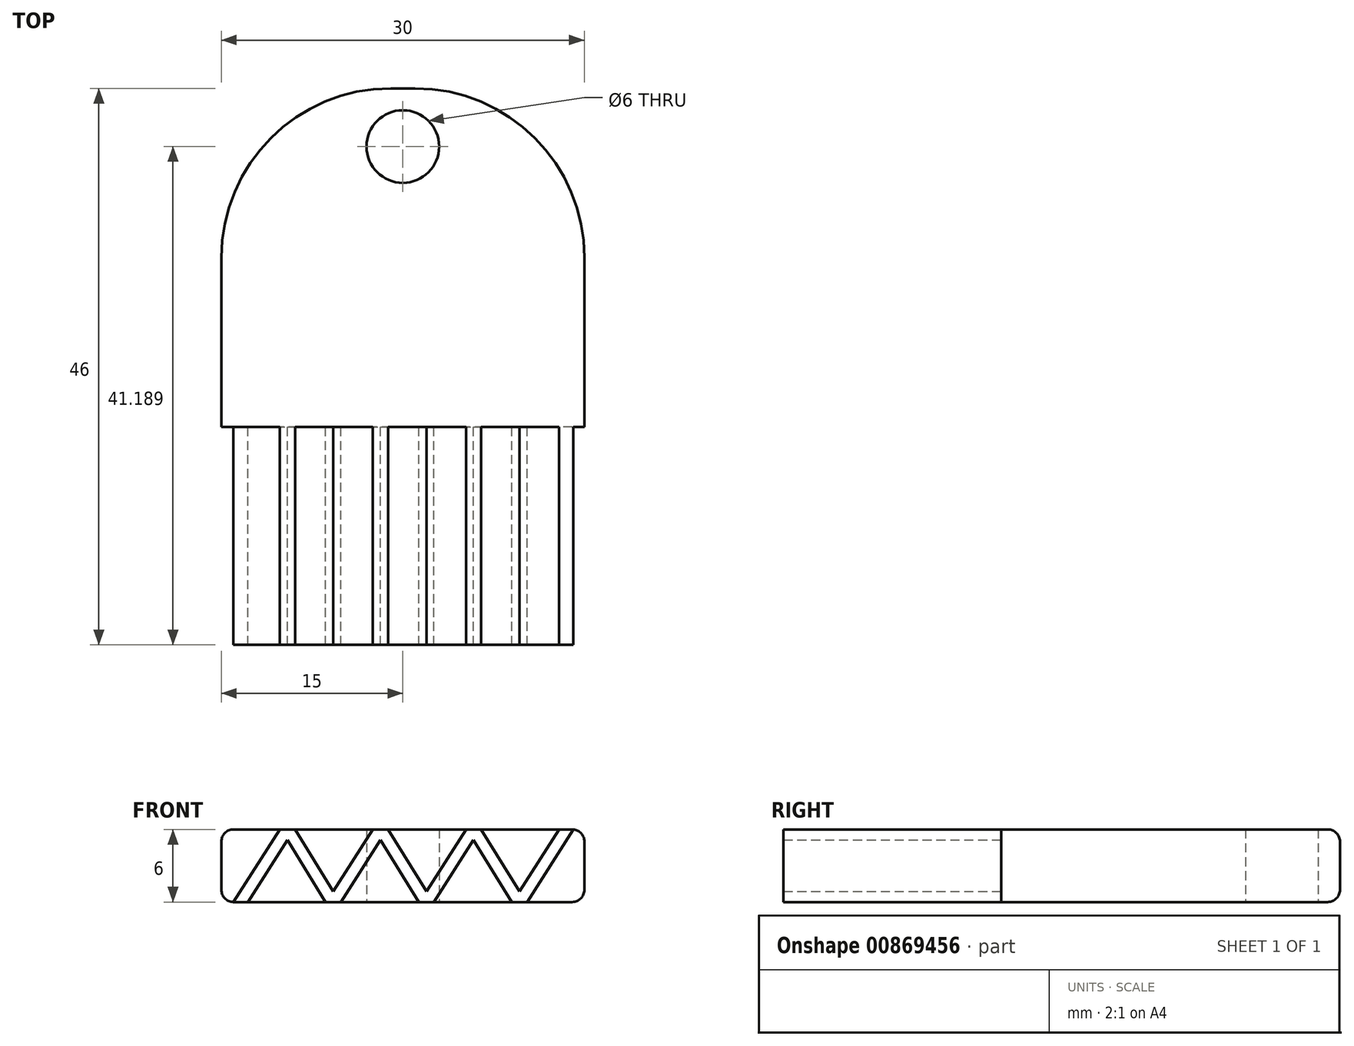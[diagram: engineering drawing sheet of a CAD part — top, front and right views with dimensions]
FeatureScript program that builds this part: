
annotation { "Feature Type Name" : "Feature", "Feature Type Description" : "" }
export const myFeature = defineFeature(function(context is Context, id is Id, definition is map)
    precondition{}
    {
        {
            var Q0;
            Q0=qCreatedBy(makeId("Top.planeOp"),FACE);
            var sketch = newSketch(context, id + "F0", { "sketchPlane" : qUnion([Q0])});
            skLineSegment(sketch, "E0.bottom", {"start": v(15, -14) * mm, "end": v(-15, -14) * mm});
            skLineSegment(sketch, "E0.top", {"start": v(1, 14) * mm, "end": v(-1, 14) * mm});
            skLineSegment(sketch, "E0.left", {"start": v(15, -14) * mm, "end": v(15, 0) * mm});
            skLineSegment(sketch, "E0.right", {"start": v(-15, -14) * mm, "end": v(-15, 0) * mm});
            skPoint(sketch, "E0.middle", {"position": v(0, 0) * mm});
            skPoint(sketch, "E1.visualSharp", {"position": v(-15, 14) * mm});
            skArc(sketch, "E1.filletArc", {"start": v(-1, 14) * mm, "mid": v(-10.9, 9.9) * mm, "end": v(-15, 0) * mm});
            skPoint(sketch, "E2.visualSharp", {"position": v(15, 14) * mm});
            skArc(sketch, "E2.filletArc", {"start": v(15, 0) * mm, "mid": v(10.9, 9.9) * mm, "end": v(1, 14) * mm});
            skCircle(sketch, "E3", {"center": v(0, 9.19) * mm, "radius": 3 * mm});
            skSolve(sketch);
        }
        {
            var Q0;
            Q0=makeQuery(id+"F0.imprint","IMPRINT",FACE,{"disambiguationData":[TD([[makeQuery(id+"F0.imprint","IMPRINT",EDGE,{"derivedFrom":sQuery(id+"F0.wireOp",EDGE,"E0.bottom")}),-1.0]])]});
            extrude(context, id + "F1", {"entities" : qUnion([Q0]), "depth" : 6 * mm});
        }
        {
            var Q0;
            Q0=makeQuery(id+"F1.opExtrude","CAP_FACE",FACE,{"disambiguationData":[OSD([sQuery(id+"F0.wireOp",EDGE,"E0.bottom"),sQuery(id+"F0.wireOp",EDGE,"E0.left"),sQuery(id+"F0.wireOp",EDGE,"E0.right"),sQuery(id+"F0.wireOp",EDGE,"E1.filletArc"),sQuery(id+"F0.wireOp",EDGE,"E2.filletArc"),sQuery(id+"F0.wireOp",EDGE,"E3")])],"isStart":false});
            var sketch = newSketch(context, id + "F2", { "sketchPlane" : qUnion([Q0])});
            skText(sketch, "E4", { "text": "Z", "fontName": "Tinos-Regular.ttf"});
            const initialGuessF2  = {"E4": [-0.00651, -0.01117, 1, 0, 0.01506]};
            skSetInitialGuess(sketch, initialGuessF2);
            skSolve(sketch);
        }
        {
            var Q0;
            Q0=makeQuery(id+"F1.opExtrude","CAP_EDGE",EDGE,{"disambiguationData":[OSD([sQuery(id+"F0.wireOp",EDGE,"E1.filletArc"),sQuery(id+"F0.wireOp",EDGE,"E2.filletArc")])],"isStart":false});
            var Q1;
            Q1=makeQuery(id+"F1.opExtrude","CAP_EDGE",EDGE,{"disambiguationData":[OSD([sQuery(id+"F0.wireOp",EDGE,"E0.right")])],"isStart":false});
            var Q2;
            Q2=makeQuery(id+"F1.opExtrude","CAP_EDGE",EDGE,{"disambiguationData":[OSD([sQuery(id+"F0.wireOp",EDGE,"E0.left")])],"isStart":false});
            var Q3;
            Q3=makeQuery(id+"F1.opExtrude","CAP_EDGE",EDGE,{"disambiguationData":[OSD([sQuery(id+"F0.wireOp",EDGE,"E0.right")])],"isStart":true});
            var Q4;
            Q4=makeQuery(id+"F1.opExtrude","CAP_EDGE",EDGE,{"disambiguationData":[OSD([sQuery(id+"F0.wireOp",EDGE,"E1.filletArc"),sQuery(id+"F0.wireOp",EDGE,"E2.filletArc")])],"isStart":true});
            var Q5;
            Q5=makeQuery(id+"F1.opExtrude","CAP_EDGE",EDGE,{"disambiguationData":[OSD([sQuery(id+"F0.wireOp",EDGE,"E0.left")])],"isStart":true});
            fillet(context, id + "F3", {"entities" : qUnion([Q0, Q1, Q2, Q3, Q4, Q5]), "radius" : 1 * mm, "tangentPropagation" : true, "allowEdgeOverflow" : false});
        }
        {
            var Q0;
            Q0=makeQuery(id+"F1.opExtrude","SWEPT_FACE",FACE,{"disambiguationData":[OSD([sQuery(id+"F0.wireOp",EDGE,"E0.bottom")])]});
            var sketch = newSketch(context, id + "F4", { "sketchPlane" : qUnion([Q0])});
            skLineSegment(sketch, "E5", {"start": v(-14, 0) * mm, "end": v(-9.53, 7) * mm});
            skLineSegment(sketch, "E6", {"start": v(-9.53, 7) * mm, "end": v(-5.75, 0.88) * mm});
            skLineSegment(sketch, "E7", {"start": v(-5.75, 0.88) * mm, "end": v(-1.84, 7) * mm});
            skLineSegment(sketch, "E8", {"start": v(-1.84, 7) * mm, "end": v(1.94, 0.88) * mm});
            skLineSegment(sketch, "E9", {"start": v(1.94, 0.88) * mm, "end": v(5.85, 7) * mm});
            skLineSegment(sketch, "E10", {"start": v(5.85, 7) * mm, "end": v(9.64, 0.88) * mm});
            skLineSegment(sketch, "E11", {"start": v(9.64, 0.88) * mm, "end": v(13.54, 7) * mm});
            skLineSegment(sketch, "E12.0", {"start": v(-12.81, 0) * mm, "end": v(-9.55, 5.12) * mm});
            skLineSegment(sketch, "E13.trimOffspring", {"start": v(-9.55, 5.12) * mm, "end": v(-5.76, -1) * mm});
            skLineSegment(sketch, "E14.0", {"start": v(-5.76, -1) * mm, "end": v(-1.86, 5.12) * mm});
            skLineSegment(sketch, "E15.0", {"start": v(-1.86, 5.12) * mm, "end": v(1.93, -1) * mm});
            skLineSegment(sketch, "E16.0", {"start": v(1.93, -1) * mm, "end": v(5.84, 5.12) * mm});
            skLineSegment(sketch, "E17.0", {"start": v(5.84, 5.12) * mm, "end": v(9.62, -1) * mm});
            skLineSegment(sketch, "E18.0", {"start": v(9.62, -1) * mm, "end": v(14.73, 7) * mm});
            skLineSegment(sketch, "E19", {"start": v(-15.07, 7) * mm, "end": v(16.42, 7) * mm});
            skLineSegment(sketch, "E20", {"start": v(-15.53, -1) * mm, "end": v(13.55, -1) * mm});
            skSolve(sketch);
        }
        {
            var Q0;
            {var subQ1=sQuery(id+"F4.wireOp",EDGE,"E12.0");Q0=makeQuery(id+"F4.imprint","IMPRINT",FACE,{"disambiguationData":[TD([[makeQuery(id+"F4.imprint","IMPRINT",EDGE,{"derivedFrom":subQ1}),1.0]])]});}
            extrude(context, id + "F5", {"entities" : qUnion([Q0]), "operationType" : NewBodyOperationType.ADD, "depth" : 18 * mm});
        }
    });
